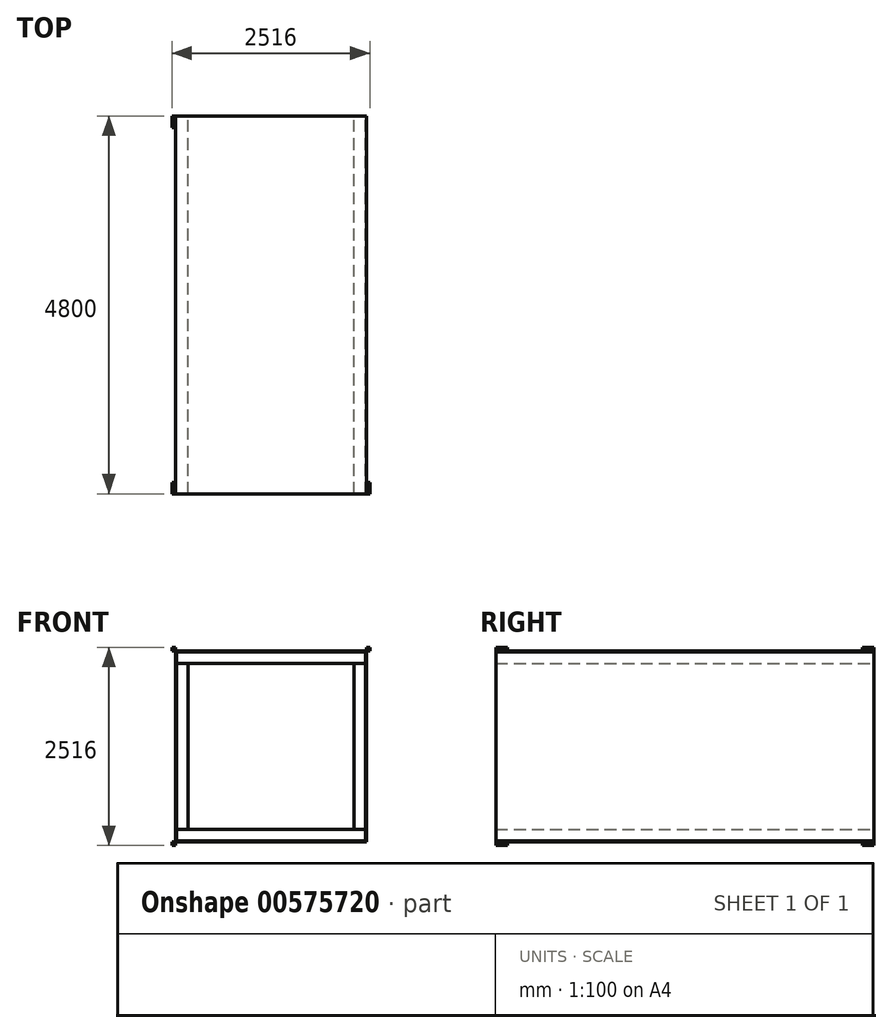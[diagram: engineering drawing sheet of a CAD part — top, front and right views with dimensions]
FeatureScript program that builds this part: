
annotation { "Feature Type Name" : "Feature", "Feature Type Description" : "" }
export const myFeature = defineFeature(function(context is Context, id is Id, definition is map)
    precondition{}
    {
        {
            var Q0;
            Q0=qCreatedBy(makeId("Front.planeOp"),FACE);
            var sketch = newSketch(context, id + "F0", { "sketchPlane" : qUnion([Q0])});
            skLineSegment(sketch, "E0.bottom", {"start": v(-639.22, 1307.93) * mm, "end": v(1760.78, 1307.93) * mm});
            skLineSegment(sketch, "E0.top", {"start": v(-639.22, -1092.07) * mm, "end": v(1760.78, -1092.07) * mm});
            skLineSegment(sketch, "E0.left", {"start": v(-639.22, 1307.93) * mm, "end": v(-639.22, -1092.07) * mm});
            skLineSegment(sketch, "E0.right", {"start": v(1760.78, 1307.93) * mm, "end": v(1760.78, -1092.07) * mm});
            skLineSegment(sketch, "E1.0", {"start": v(-494.22, 1162.93) * mm, "end": v(1615.78, 1162.93) * mm});
            skLineSegment(sketch, "E1.1", {"start": v(-494.22, 1162.93) * mm, "end": v(-494.22, -947.07) * mm});
            skLineSegment(sketch, "E1.2", {"start": v(-494.22, -947.07) * mm, "end": v(1615.78, -947.07) * mm});
            skLineSegment(sketch, "E1.3", {"start": v(1615.78, 1162.93) * mm, "end": v(1615.78, -947.07) * mm});
            skLineSegment(sketch, "E2", {"start": v(-494.22, -947.07) * mm, "end": v(-639.22, -947.07) * mm});
            skLineSegment(sketch, "E3", {"start": v(1615.78, -947.07) * mm, "end": v(1760.78, -947.07) * mm});
            skLineSegment(sketch, "E4", {"start": v(-494.22, 1162.93) * mm, "end": v(-639.22, 1162.93) * mm});
            skLineSegment(sketch, "E5", {"start": v(1615.78, 1162.93) * mm, "end": v(1760.78, 1162.93) * mm});
            skLineSegment(sketch, "E6.0", {"start": v(-652.22, 1320.93) * mm, "end": v(1773.78, 1320.93) * mm});
            skLineSegment(sketch, "E6.1", {"start": v(-652.22, 1320.93) * mm, "end": v(-652.22, -1105.07) * mm});
            skLineSegment(sketch, "E6.2", {"start": v(-652.22, -1105.07) * mm, "end": v(1773.78, -1105.07) * mm});
            skLineSegment(sketch, "E6.3", {"start": v(1773.78, 1320.93) * mm, "end": v(1773.78, -1105.07) * mm});
            skLineSegment(sketch, "E7", {"start": v(-639.22, 1307.93) * mm, "end": v(-652.22, 1307.93) * mm});
            skLineSegment(sketch, "E8", {"start": v(1760.78, 1307.93) * mm, "end": v(1773.78, 1307.93) * mm});
            skLineSegment(sketch, "E9", {"start": v(1760.78, -1092.07) * mm, "end": v(1773.78, -1092.07) * mm});
            skLineSegment(sketch, "E10", {"start": v(-639.22, -1092.07) * mm, "end": v(-652.22, -1092.07) * mm});
            skSolve(sketch);
        }
        {
            var Q0;
            Q0=makeQuery(id+"F0.imprint","IMPRINT",FACE,{"disambiguationData":[TD([[makeQuery(id+"F0.imprint","IMPRINT",EDGE,{"derivedFrom":sQuery(id+"F0.wireOp",EDGE,"E0.bottom")}),-1.0]])]});
            var Q1;
            {var subQ1=sQuery(id+"F0.wireOp",EDGE,"E0.top");Q1=makeQuery(id+"F0.imprint","IMPRINT",FACE,{"disambiguationData":[TD([[makeQuery(id+"F0.imprint","IMPRINT",EDGE,{"derivedFrom":subQ1}),1.0]])]});}
            extrude(context, id + "F1", {"entities" : qUnion([Q0, Q1]), "depth" : 4800 * mm, "offsetDistance" : 25 * mm});
        }
        {
            var Q0;
            Q0=makeQuery(id+"F0.imprint","IMPRINT",FACE,{"disambiguationData":[TD([[makeQuery(id+"F0.imprint","IMPRINT",EDGE,{"derivedFrom":sQuery(id+"F0.wireOp",EDGE,"E1.1")}),-1.0]])]});
            var Q1;
            Q1=makeQuery(id+"F0.imprint","IMPRINT",FACE,{"disambiguationData":[TD([[makeQuery(id+"F0.imprint","IMPRINT",EDGE,{"derivedFrom":sQuery(id+"F0.wireOp",EDGE,"E1.3")}),1.0]])]});
            extrude(context, id + "F2", {"entities" : qUnion([Q0, Q1]), "depth" : 4800 * mm, "offsetDistance" : 25 * mm});
        }
        {
            var Q0;
            Q0=makeQuery(id+"F0.imprint","IMPRINT",FACE,{"disambiguationData":[TD([[makeQuery(id+"F0.imprint","IMPRINT",EDGE,{"derivedFrom":sQuery(id+"F0.wireOp",EDGE,"E0.bottom")}),1.0]])]});
            var Q1;
            Q1=makeQuery(id+"F0.imprint","IMPRINT",FACE,{"disambiguationData":[TD([[makeQuery(id+"F0.imprint","IMPRINT",EDGE,{"derivedFrom":sQuery(id+"F0.wireOp",EDGE,"E0.top")}),-1.0]])]});
            extrude(context, id + "F3", {"entities" : qUnion([Q0, Q1]), "depth" : 4800 * mm, "offsetDistance" : 25 * mm});
        }
        {
            var Q0;
            {var subQ3=sQuery(id+"F0.wireOp",EDGE,"E7");Q0=makeQuery(id+"F0.imprint","IMPRINT",FACE,{"disambiguationData":[TD([[makeQuery(id+"F0.imprint","IMPRINT",EDGE,{"derivedFrom":subQ3}),1.0]])]});}
            var Q1;
            {var subQ0=sQuery(id+"F0.wireOp",EDGE,"E8");Q1=makeQuery(id+"F0.imprint","IMPRINT",FACE,{"disambiguationData":[TD([[makeQuery(id+"F0.imprint","IMPRINT",EDGE,{"derivedFrom":subQ0}),-1.0]])]});}
            extrude(context, id + "F4", {"entities" : qUnion([Q0, Q1]), "depth" : 4800 * mm, "offsetDistance" : 25 * mm});
        }
        {
            var Q0;
            Q0=makeQuery(id+"F3.opExtrude","SWEPT_FACE",FACE,{"disambiguationData":[OSD([sQuery(id+"F0.wireOp",EDGE,"E6.0")])]});
            var sketch = newSketch(context, id + "F5", { "sketchPlane" : qUnion([Q0])});
            skLineSegment(sketch, "E11.bottom", {"start": v(-652.22, -4800) * mm, "end": v(1818.78, -4800) * mm});
            skLineSegment(sketch, "E11.top", {"start": v(-652.22, -4655) * mm, "end": v(1818.78, -4655) * mm});
            skLineSegment(sketch, "E11.left", {"start": v(-652.22, -4800) * mm, "end": v(-652.22, -4655) * mm});
            skLineSegment(sketch, "E11.right", {"start": v(1818.78, -4800) * mm, "end": v(1818.78, -4655) * mm});
            skLineSegment(sketch, "E12.bottom", {"start": v(-652.22, -4800) * mm, "end": v(-697.22, -4800) * mm});
            skLineSegment(sketch, "E12.top", {"start": v(-652.22, -4655) * mm, "end": v(-697.22, -4655) * mm});
            skLineSegment(sketch, "E12.right", {"start": v(-697.22, -4800) * mm, "end": v(-697.22, -4655) * mm});
            skSolve(sketch);
        }
        {
            var Q0;
            {var subQ0=sQuery(id+"F5.wireOp",EDGE,"E11.left");Q0=makeQuery(id+"F5.imprint","IMPRINT",FACE,{"disambiguationData":[TD([[makeQuery(id+"F5.imprint","IMPRINT",EDGE,{"derivedFrom":subQ0}),-1.0]])]});}
            var Q1;
            Q1=makeQuery(id+"F5.imprint","IMPRINT",FACE,{"disambiguationData":[TD([[makeQuery(id+"F5.imprint","IMPRINT",EDGE,{"derivedFrom":sQuery(id+"F5.wireOp",EDGE,"E12.bottom")}),-1.0]])]});
            var Q2;
            {var subQ3=sQuery(id+"F5.wireOp",EDGE,"E11.right");Q2=makeQuery(id+"F5.imprint","IMPRINT",FACE,{"disambiguationData":[TD([[makeQuery(id+"F5.imprint","IMPRINT",EDGE,{"derivedFrom":subQ3}),1.0]])]});}
            extrude(context, id + "F6", {"entities" : qUnion([Q0, Q1, Q2]), "depth" : 45 * mm, "offsetDistance" : 25 * mm});
        }
        {
            var Q0;
            Q0=makeQuery(id+"F6.opExtrude","SWEPT_BODY",BODY,{"disambiguationData":[OSD([sQuery(id+"F5.wireOp",EDGE,"E11.bottom"),sQuery(id+"F5.wireOp",EDGE,"E11.top"),sQuery(id+"F5.wireOp",EDGE,"E11.right"),sQuery(id+"F5.wireOp",EDGE,"E12.bottom"),sQuery(id+"F5.wireOp",EDGE,"E12.top"),sQuery(id+"F5.wireOp",EDGE,"E12.right")])]});
            var Q1;
            Q1=makeQuery(id+"F3.opExtrude","SWEPT_FACE",FACE,{"disambiguationData":[OSD([sQuery(id+"F0.wireOp",EDGE,"E6.2")])]});
            transform(context, id + "F7", {"entities" : qUnion([Q0]), "transformType" : TransformType.TRANSLATION_DISTANCE, "transformDirection" : qUnion([Q1]), "distance" : 2471 * mm, "makeCopy" : true});
        }
        {
            var Q0;
            Q0=makeQuery(id+"F6.opExtrude","SWEPT_BODY",BODY,{"disambiguationData":[OSD([sQuery(id+"F5.wireOp",EDGE,"E11.bottom"),sQuery(id+"F5.wireOp",EDGE,"E11.top"),sQuery(id+"F5.wireOp",EDGE,"E11.right"),sQuery(id+"F5.wireOp",EDGE,"E12.bottom"),sQuery(id+"F5.wireOp",EDGE,"E12.top"),sQuery(id+"F5.wireOp",EDGE,"E12.right")])]});
            var Q1;
            Q1=makeQuery(id+"F7.opPattern","COPY",BODY,{"derivedFrom":makeQuery(id+"F6.opExtrude","SWEPT_BODY",BODY,{"disambiguationData":[OSD([sQuery(id+"F5.wireOp",EDGE,"E11.bottom"),sQuery(id+"F5.wireOp",EDGE,"E11.top"),sQuery(id+"F5.wireOp",EDGE,"E11.right"),sQuery(id+"F5.wireOp",EDGE,"E12.bottom"),sQuery(id+"F5.wireOp",EDGE,"E12.top"),sQuery(id+"F5.wireOp",EDGE,"E12.right")])]}),"instanceName":"1"});
            var Q2;
            Q2=makeQuery(id+"F6.opExtrude","SWEPT_FACE",FACE,{"disambiguationData":[OSD([sQuery(id+"F5.wireOp",EDGE,"E11.top"),sQuery(id+"F5.wireOp",EDGE,"E12.top")])]});
            transform(context, id + "F8", {"entities" : qUnion([Q0, Q1]), "transformType" : TransformType.TRANSLATION_DISTANCE, "transformDirection" : qUnion([Q2]), "distance" : 4655 * mm, "makeCopy" : true});
        }
    });
